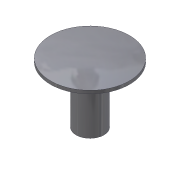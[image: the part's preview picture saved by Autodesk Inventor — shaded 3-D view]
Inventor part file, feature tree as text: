
AUTODESK INVENTOR PART (.ipt)
format: ipt  version: 2013 (Build 170138000, 138)  size: 92,160 bytes
history: native  units: mm (DEFAULTED — no unit token found)
features: sketch x2, reference x2, revolve x1, extrude x1
ambient origin geometry x8: Origin, YZ Plane, XZ Plane, XY Plane, X Axis, Y Axis, Z Axis, Center Point
bodies: Solid1 (feature_tree)
feature tree (6):
  revolve  "Revolution1"  [1 undecoded]
  extrude  "Extrusion1"  [1 undecoded]
  sketch  "Sketch1"  dims[d0=90.0deg d1=3.175mm d2=0.0mm]
  reference  "Reference1"
  reference  "Reference2"
  sketch  "Sketch2"
note: 2 required parameter values undecoded (feature->parameter linkage not recoverable at this tier; creation-order binding heuristic only, values carry confidence <= 0.55)